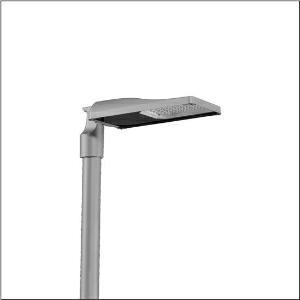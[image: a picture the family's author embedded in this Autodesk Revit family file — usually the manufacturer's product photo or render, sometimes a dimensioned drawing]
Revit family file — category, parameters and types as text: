
# Revit family: streetlight_sl_31_mini___st1_0a_5xh2d31a08ga_4fc3
name_source: partatom
category: Lighting Fixtures
units: mm (PartAtom-declared; Revit-internal decimal feet)

## family parameters
Cut with Voids When Loaded = No
Host = Face
Light Source = No
Part Type = Normal
Room Calculation Point = No
Round Connector Dimension = Use Diameter
Shared = No

## types (1)
- --- (1 x LED, 5710 lm, 37.3 W, 3000K)
    Apparent Load = 37 VA
    CIE Flux Codes = 37 72 97 100 100
    Color Rendering = 70
    Color Temperature = 3000K
    Default Elevation = 1800 mm
    Description = Streetlight SL 31 mini, mast luminaire, primary light control with lens, of PMMA, primary optical cover: cover, of toughened safety glass, transparent, light distribution: ST1.0a, light emission: direct distribution, primary light characteristic: asymmetric, installation type: post-top, side-entry, LED, High Power LED, rated luminous flux: 5.710lm, luminous efficacy: 153lm/W, light colour: 730, colour temperature: 3000K, control: presetting dimming linear, flexible luminous flux parameterisation, time-dependent luminous flux control, constant luminous flux control, intelligent temperature release in ECG and LED module, overheat protection, with cable H07RN-F 2x 1.5mm², mains connection: 220..240V, AC, 50/60Hz, connection cable pre-assembled, cable length: 6,5m, start of lifetime: 37W, end of service life: 39W, reduction: 18W, luminaire housing, of diecast aluminium, powder-coated, Siteco® metallic grey (DB 702S), corrosivity category C5 high according to DIN EN ISO 12944, no sealing on luminaire upper side, inclination: -15°..+20° (post-top) | -20°..+20° (side-entry), adjustable in 5° steps, mast flange (76/60mm) included as standard, multi-level sealing system, sealing non-destructively replaceable, protection rating (complete): IP66, insulation class (complete): insulation class II (safety insulation), certification: CE, ENEC, ENEC+, VDE, UKCA, impact resistance: IK09, permissible operating ambient temperature for outdoor applications: -40..+50°C, standard-compliant lighting for roads and squares, packaging unit: 1 piece

Light Distribution: ST1.0a
    Height = 76 mm
    Lamp = 1 x LED
    Lamp Light Flux = 5710 lm
    Lamp Power = 37.3 W
    Lamp count = 1
    Length = 547 mm
    Luminous efficacy = 153 lm/W
    Manufacturer = Siteco
    ModVariant = No
    Model = 5XH2D31A08GA
    Number of Poles = 1
    OnlyDefault = Yes
    Power Factor = 1
    Product Name = Streetlight SL 31 mini | ST1.0a
    Product group = mast luminaire | pylon top
    ProductGroupID = 6100
    Protection Class = Protection class II
    Protection Degree = IP 66
    RLX_Detail_Level = 1
    RLX_Emergency_Light_Flux = 0 lm
    RLX_Emergency_Type = 0
    RLX_Emergency_Type_DB = No
    RlxData = <blob elided: 39685 chars, md5=0d20160a>
    Socket = socket
    Standby Power = 0 W
    System Light Flux = 5710 lm
    System Power = 37 W
    Type Comments = factory setting: luminous flux: 100 % | dim-lin: 254 | 386 mA
    Type Image = l_1300326.jpg
    URL = http://relux.com
    VarID = @adj_013625
    Voltage = 0 V
    Weight = 0.00 kg
    Width = 265 mm

## geometry (parser evidence)
native form markers: Blend x4, Sweep x10
no freeform markers — native parametric forms only
